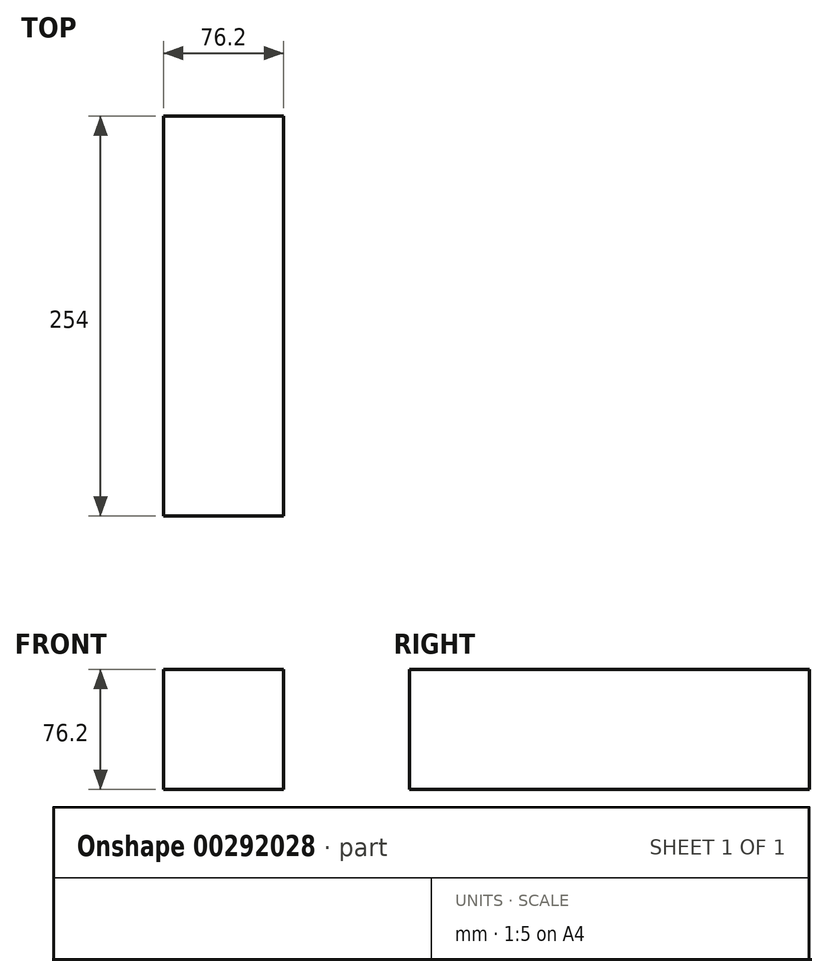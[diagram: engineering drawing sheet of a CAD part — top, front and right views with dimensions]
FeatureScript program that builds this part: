
annotation { "Feature Type Name" : "Feature", "Feature Type Description" : "" }
export const myFeature = defineFeature(function(context is Context, id is Id, definition is map)
    precondition{}
    {
        {
            var Q0;
            Q0=qCreatedBy(makeId("Front.planeOp"),FACE);
            var sketch = newSketch(context, id + "F0", { "sketchPlane" : qUnion([Q0])});
            skLineSegment(sketch, "E0.bottom", {"start": v(0, 0) * mm, "end": v(76.2, 0) * mm});
            skLineSegment(sketch, "E0.top", {"start": v(0, 76.2) * mm, "end": v(76.2, 76.2) * mm});
            skLineSegment(sketch, "E0.left", {"start": v(0, 0) * mm, "end": v(0, 76.2) * mm});
            skLineSegment(sketch, "E0.right", {"start": v(76.2, 0) * mm, "end": v(76.2, 76.2) * mm});
            skSolve(sketch);
        }
        {
            var Q0;
            Q0 = qSketchRegion(id + "F0", true);
            extrude(context, id + "F1", {"entities" : qUnion([Q0]), "depth" : 254 * mm});
        }
        {
            var Q0;
            Q0=makeQuery(id+"F1.opExtrude","CAP_FACE",FACE,{"disambiguationData":[OSD([sQuery(id+"F0.wireOp",EDGE,"E0.bottom"),sQuery(id+"F0.wireOp",EDGE,"E0.top"),sQuery(id+"F0.wireOp",EDGE,"E0.left"),sQuery(id+"F0.wireOp",EDGE,"E0.right")])],"isStart":false});
            var sketch = newSketch(context, id + "F2", { "sketchPlane" : qUnion([Q0])});
            skCircle(sketch, "E1", {"center": v(38.1, 38.1) * mm, "radius": 12.7 * mm});
            skSolve(sketch);
        }
        {
            var Q0;
            Q0=makeQuery(id+"F2.imprint","IMPRINT",FACE,{"disambiguationData":[TD([[makeQuery(id+"F2.imprint","IMPRINT",EDGE,{"derivedFrom":sQuery(id+"F2.wireOp",EDGE,"E1")}),1.0]])]});
            extrude(context, id + "F3", {"entities" : qUnion([Q0]), "operationType" : NewBodyOperationType.ADD, "oppositeDirection" : true, "depth" : 25.4 * mm});
        }
    });
